# Revit family: RN 80035 Optipress-Aquaplus-Übergang
name_source: partatom
category: Rohrformteile
units: mm (PartAtom-declared; Revit-internal decimal feet)

## family parameters
Arbeitsebenenbasiert = Nein
Beim Laden mit Abzugskörper schneiden = Nein
Bemaßung runder Anschluss = Durchmesser verwenden
Gemeinsam genutzt = Nein
Immer vertikal = Ja
Teiletyp = Verbindung

## types (21) — shared parameters
1.010.00.2 Blattnummer der Richtlinie = 29
1.010.00.3 Ausgabedatum (Monat) der Richtlinie = 201308
1.010.00.4 Herstellername = R. Nussbaum AG
1.010.00.5 Revisionsdatum der Datei = 20190521
1.010.00.6 Webadresse des Herstellers = http://www.nussbaum.ch
1.100.00.4 Produktbezeichnung = Versorgung
1.110.00.2 Index = 4
1.110.00.4 Produktbezeichnung = Optipress
1.960/3L.00.8 Link (URL) = https://www.nussbaum.ch
29.700.00.4 Produktname = Optipress-Aquaplus-Übergang, mit Aussengewinde
29.700.00.5 Produktkennung = 2
29.700.00.6 Querschnittsform = 1
29.700.00.7 Nennweitensystem = DN
29.700.00.8 Nenndrucksystem = PN
29.710.02.4 Nenndruck = 16
29.710.02.5 max. zul. Überdruck [hPa] = 1600
29.710.02.7 max. zul. Dauer-Betriebsdruck [hPa] = 1600
29.710.02.9 max. zul. Dauer-Betriebstemperatur [°C] = 95
Connector Visibility = Nein
EnclosingSpace Visibility = Nein

## per-type parameters (varying)
- 80035.21, Optipress-Aquaplus-Übergang, mit Aussengewinde, DN=12x15, L=53, R=½: 1.800.00.3 TGA-Nummer=01900400000000000000000000000000000000000000000024000000000000000001; 1.810.00.3 Hersteller-Bestellnummer=80035.21; 1.810.00.4 DATANORM-Nummer=80035.21; 1.810.00.5 StLB-Nummer=267.112; 1.810.00.6 GTIN-Nummer=7612945051660; 29.710.02.10 Formstück-Gewicht [kg]=0.047; 29.710.02.3 Benennung=Optipress-Aquaplus-Übergang, mit Aussengewinde, DN=12x15, L=53, R=½; CONNECTOR0_DIAMETER_dX_0r=12 mm  [stored 0.0393701 ft]; CONNECTOR0_dX_01=22 mm; CONNECTOR0_ref_dX=22 mm; CONNECTOR1_DIAMETER_dX_0r=15 mm  [stored 0.0492126 ft]; CONNECTOR1_dX_00=40 mm  [stored 0.131234 ft]; CONNECTOR1_dX_01=53 mm; CONNECTOR1_ref_dX=40 mm  [stored 0.131234 ft]; R. Nussbaum AG 80035.21 de Visibility=Ja; R. Nussbaum AG 80035.22 de Visibility=Nein; R. Nussbaum AG 80035.23 de Visibility=Nein; R. Nussbaum AG 80035.24 de Visibility=Nein; R. Nussbaum AG 80035.25 de Visibility=Nein; R. Nussbaum AG 80035.27 de Visibility=Nein; R. Nussbaum AG 80035.28 de Visibility=Nein; R. Nussbaum AG 80035.29 de Visibility=Nein; R. Nussbaum AG 80035.30 de Visibility=Nein; R. Nussbaum AG 80035.31 de Visibility=Nein; R. Nussbaum AG 80035.32 de Visibility=Nein; R. Nussbaum AG 80035.33 de Visibility=Nein; R. Nussbaum AG 80035.34 de Visibility=Nein; R. Nussbaum AG 80035.35 de Visibility=Nein; R. Nussbaum AG 80035.36 de Visibility=Nein; R. Nussbaum AG 80035.37 de Visibility=Nein; R. Nussbaum AG 80035.38 de Visibility=Nein; R. Nussbaum AG 80035.70 de Visibility=Nein; R. Nussbaum AG 80035.71 de Visibility=Nein; R. Nussbaum AG 80035.72 de Visibility=Nein; R. Nussbaum AG 80035.73 de Visibility=Nein
- 80035.22, Optipress-Aquaplus-Übergang, mit Aussengewinde, DN=15x20, L=56, R=¾: 1.800.00.3 TGA-Nummer=01900400000000000000000000000000000000000000000024000000000000000002; 1.810.00.3 Hersteller-Bestellnummer=80035.22; 1.810.00.4 DATANORM-Nummer=80035.22; 1.810.00.6 GTIN-Nummer=7612945051677; 29.710.02.10 Formstück-Gewicht [kg]=0.058; 29.710.02.3 Benennung=Optipress-Aquaplus-Übergang, mit Aussengewinde, DN=15x20, L=56, R=¾; CONNECTOR0_DIAMETER_dX_0r=15 mm  [stored 0.0492126 ft]; CONNECTOR0_dX_01=22 mm; CONNECTOR0_ref_dX=22 mm; CONNECTOR1_DIAMETER_dX_0r=20 mm; CONNECTOR1_dX_00=41 mm  [stored 0.134514 ft]; CONNECTOR1_dX_01=56 mm; CONNECTOR1_ref_dX=41 mm  [stored 0.134514 ft]; R. Nussbaum AG 80035.21 de Visibility=Nein; R. Nussbaum AG 80035.22 de Visibility=Ja; R. Nussbaum AG 80035.23 de Visibility=Nein; R. Nussbaum AG 80035.24 de Visibility=Nein; R. Nussbaum AG 80035.25 de Visibility=Nein; R. Nussbaum AG 80035.27 de Visibility=Nein; R. Nussbaum AG 80035.28 de Visibility=Nein; R. Nussbaum AG 80035.29 de Visibility=Nein; R. Nussbaum AG 80035.30 de Visibility=Nein; R. Nussbaum AG 80035.31 de Visibility=Nein; R. Nussbaum AG 80035.32 de Visibility=Nein; R. Nussbaum AG 80035.33 de Visibility=Nein; R. Nussbaum AG 80035.34 de Visibility=Nein; R. Nussbaum AG 80035.35 de Visibility=Nein; R. Nussbaum AG 80035.36 de Visibility=Nein; R. Nussbaum AG 80035.37 de Visibility=Nein; R. Nussbaum AG 80035.38 de Visibility=Nein; R. Nussbaum AG 80035.70 de Visibility=Nein; R. Nussbaum AG 80035.71 de Visibility=Nein; R. Nussbaum AG 80035.72 de Visibility=Nein; R. Nussbaum AG 80035.73 de Visibility=Nein
- 80035.23, Optipress-Aquaplus-Übergang, mit Aussengewinde, DN=15, L=52, R=½: 1.800.00.3 TGA-Nummer=01900400000000000000000000000000000000000000000024000000000000000003; 1.810.00.3 Hersteller-Bestellnummer=80035.23; 1.810.00.4 DATANORM-Nummer=80035.23; 1.810.00.5 StLB-Nummer=267.113; 1.810.00.6 GTIN-Nummer=7612945051684; 29.710.02.10 Formstück-Gewicht [kg]=0.049; 29.710.02.3 Benennung=Optipress-Aquaplus-Übergang, mit Aussengewinde, DN=15, L=52, R=½; CONNECTOR0_DIAMETER_dX_0r=15 mm  [stored 0.0492126 ft]; CONNECTOR0_dX_01=22 mm; CONNECTOR0_ref_dX=22 mm; CONNECTOR1_DIAMETER_dX_0r=15 mm  [stored 0.0492126 ft]; CONNECTOR1_dX_00=39 mm; CONNECTOR1_dX_01=52 mm; CONNECTOR1_ref_dX=39 mm; R. Nussbaum AG 80035.21 de Visibility=Nein; R. Nussbaum AG 80035.22 de Visibility=Nein; R. Nussbaum AG 80035.23 de Visibility=Ja; R. Nussbaum AG 80035.24 de Visibility=Nein; R. Nussbaum AG 80035.25 de Visibility=Nein; R. Nussbaum AG 80035.27 de Visibility=Nein; R. Nussbaum AG 80035.28 de Visibility=Nein; R. Nussbaum AG 80035.29 de Visibility=Nein; R. Nussbaum AG 80035.30 de Visibility=Nein; R. Nussbaum AG 80035.31 de Visibility=Nein; R. Nussbaum AG 80035.32 de Visibility=Nein; R. Nussbaum AG 80035.33 de Visibility=Nein; R. Nussbaum AG 80035.34 de Visibility=Nein; R. Nussbaum AG 80035.35 de Visibility=Nein; R. Nussbaum AG 80035.36 de Visibility=Nein; R. Nussbaum AG 80035.37 de Visibility=Nein; R. Nussbaum AG 80035.38 de Visibility=Nein; R. Nussbaum AG 80035.70 de Visibility=Nein; R. Nussbaum AG 80035.71 de Visibility=Nein; R. Nussbaum AG 80035.72 de Visibility=Nein; R. Nussbaum AG 80035.73 de Visibility=Nein
- 80035.24, Optipress-Aquaplus-Übergang, mit Aussengewinde, DN=15x20, L=55, R=¾: 1.800.00.3 TGA-Nummer=01900400000000000000000000000000000000000000000024000000000000000004; 1.810.00.3 Hersteller-Bestellnummer=80035.24; 1.810.00.4 DATANORM-Nummer=80035.24; 1.810.00.6 GTIN-Nummer=7612945051691; 29.710.02.10 Formstück-Gewicht [kg]=0.064; 29.710.02.3 Benennung=Optipress-Aquaplus-Übergang, mit Aussengewinde, DN=15x20, L=55, R=¾; CONNECTOR0_DIAMETER_dX_0r=15 mm  [stored 0.0492126 ft]; CONNECTOR0_dX_01=22 mm; CONNECTOR0_ref_dX=22 mm; CONNECTOR1_DIAMETER_dX_0r=20 mm; CONNECTOR1_dX_00=40 mm  [stored 0.131234 ft]; CONNECTOR1_dX_01=55 mm; CONNECTOR1_ref_dX=40 mm  [stored 0.131234 ft]; R. Nussbaum AG 80035.21 de Visibility=Nein; R. Nussbaum AG 80035.22 de Visibility=Nein; R. Nussbaum AG 80035.23 de Visibility=Nein; R. Nussbaum AG 80035.24 de Visibility=Ja; R. Nussbaum AG 80035.25 de Visibility=Nein; R. Nussbaum AG 80035.27 de Visibility=Nein; R. Nussbaum AG 80035.28 de Visibility=Nein; R. Nussbaum AG 80035.29 de Visibility=Nein; R. Nussbaum AG 80035.30 de Visibility=Nein; R. Nussbaum AG 80035.31 de Visibility=Nein; R. Nussbaum AG 80035.32 de Visibility=Nein; R. Nussbaum AG 80035.33 de Visibility=Nein; R. Nussbaum AG 80035.34 de Visibility=Nein; R. Nussbaum AG 80035.35 de Visibility=Nein; R. Nussbaum AG 80035.36 de Visibility=Nein; R. Nussbaum AG 80035.37 de Visibility=Nein; R. Nussbaum AG 80035.38 de Visibility=Nein; R. Nussbaum AG 80035.70 de Visibility=Nein; R. Nussbaum AG 80035.71 de Visibility=Nein; R. Nussbaum AG 80035.72 de Visibility=Nein; R. Nussbaum AG 80035.73 de Visibility=Nein
- 80035.25, Optipress-Aquaplus-Übergang, mit Aussengewinde, DN=20, L=56, R=¾: 1.800.00.3 TGA-Nummer=01900400000000000000000000000000000000000000000024000000000000000005; 1.810.00.3 Hersteller-Bestellnummer=80035.25; 1.810.00.4 DATANORM-Nummer=80035.25; 1.810.00.5 StLB-Nummer=267.114; 1.810.00.6 GTIN-Nummer=7612945051714; 29.710.02.10 Formstück-Gewicht [kg]=0.069; 29.710.02.3 Benennung=Optipress-Aquaplus-Übergang, mit Aussengewinde, DN=20, L=56, R=¾; CONNECTOR0_DIAMETER_dX_0r=20 mm; CONNECTOR0_dX_01=24 mm; CONNECTOR0_ref_dX=24 mm; CONNECTOR1_DIAMETER_dX_0r=20 mm; CONNECTOR1_dX_00=41 mm  [stored 0.134514 ft]; CONNECTOR1_dX_01=56 mm; CONNECTOR1_ref_dX=41 mm  [stored 0.134514 ft]; R. Nussbaum AG 80035.21 de Visibility=Nein; R. Nussbaum AG 80035.22 de Visibility=Nein; R. Nussbaum AG 80035.23 de Visibility=Nein; R. Nussbaum AG 80035.24 de Visibility=Nein; R. Nussbaum AG 80035.25 de Visibility=Ja; R. Nussbaum AG 80035.27 de Visibility=Nein; R. Nussbaum AG 80035.28 de Visibility=Nein; R. Nussbaum AG 80035.29 de Visibility=Nein; R. Nussbaum AG 80035.30 de Visibility=Nein; R. Nussbaum AG 80035.31 de Visibility=Nein; R. Nussbaum AG 80035.32 de Visibility=Nein; R. Nussbaum AG 80035.33 de Visibility=Nein; R. Nussbaum AG 80035.34 de Visibility=Nein; R. Nussbaum AG 80035.35 de Visibility=Nein; R. Nussbaum AG 80035.36 de Visibility=Nein; R. Nussbaum AG 80035.37 de Visibility=Nein; R. Nussbaum AG 80035.38 de Visibility=Nein; R. Nussbaum AG 80035.70 de Visibility=Nein; R. Nussbaum AG 80035.71 de Visibility=Nein; R. Nussbaum AG 80035.72 de Visibility=Nein; R. Nussbaum AG 80035.73 de Visibility=Nein
- 80035.27, Optipress-Aquaplus-Übergang, mit Aussengewinde, DN=20x25, L=59, R=1: 1.800.00.3 TGA-Nummer=01900400000000000000000000000000000000000000000024000000000000000006; 1.810.00.3 Hersteller-Bestellnummer=80035.27; 1.810.00.4 DATANORM-Nummer=80035.27; 1.810.00.6 GTIN-Nummer=7612945051721; 29.710.02.10 Formstück-Gewicht [kg]=0.113; 29.710.02.3 Benennung=Optipress-Aquaplus-Übergang, mit Aussengewinde, DN=20x25, L=59, R=1; CONNECTOR0_DIAMETER_dX_0r=20 mm; CONNECTOR0_dX_01=24 mm; CONNECTOR0_ref_dX=24 mm; CONNECTOR1_DIAMETER_dX_0r=25 mm  [stored 0.082021 ft]; CONNECTOR1_dX_00=43 mm  [stored 0.141076 ft]; CONNECTOR1_dX_01=60 mm; CONNECTOR1_ref_dX=43 mm  [stored 0.141076 ft]; R. Nussbaum AG 80035.21 de Visibility=Nein; R. Nussbaum AG 80035.22 de Visibility=Nein; R. Nussbaum AG 80035.23 de Visibility=Nein; R. Nussbaum AG 80035.24 de Visibility=Nein; R. Nussbaum AG 80035.25 de Visibility=Nein; R. Nussbaum AG 80035.27 de Visibility=Ja; R. Nussbaum AG 80035.28 de Visibility=Nein; R. Nussbaum AG 80035.29 de Visibility=Nein; R. Nussbaum AG 80035.30 de Visibility=Nein; R. Nussbaum AG 80035.31 de Visibility=Nein; R. Nussbaum AG 80035.32 de Visibility=Nein; R. Nussbaum AG 80035.33 de Visibility=Nein; R. Nussbaum AG 80035.34 de Visibility=Nein; R. Nussbaum AG 80035.35 de Visibility=Nein; R. Nussbaum AG 80035.36 de Visibility=Nein; R. Nussbaum AG 80035.37 de Visibility=Nein; R. Nussbaum AG 80035.38 de Visibility=Nein; R. Nussbaum AG 80035.70 de Visibility=Nein; R. Nussbaum AG 80035.71 de Visibility=Nein; R. Nussbaum AG 80035.72 de Visibility=Nein; R. Nussbaum AG 80035.73 de Visibility=Nein
- 80035.28, Optipress-Aquaplus-Übergang, mit Aussengewinde, DN=25x20, L=57, R=¾: 1.800.00.3 TGA-Nummer=01900400000000000000000000000000000000000000000024000000000000000007; 1.810.00.3 Hersteller-Bestellnummer=80035.28; 1.810.00.4 DATANORM-Nummer=80035.28; 1.810.00.6 GTIN-Nummer=7612945051738; 29.710.02.10 Formstück-Gewicht [kg]=0.079; 29.710.02.3 Benennung=Optipress-Aquaplus-Übergang, mit Aussengewinde, DN=25x20, L=57, R=¾; CONNECTOR0_DIAMETER_dX_0r=25 mm  [stored 0.082021 ft]; CONNECTOR0_dX_01=24 mm; CONNECTOR0_ref_dX=24 mm; CONNECTOR1_DIAMETER_dX_0r=20 mm; CONNECTOR1_dX_00=42 mm; CONNECTOR1_dX_01=57 mm; CONNECTOR1_ref_dX=42 mm; R. Nussbaum AG 80035.21 de Visibility=Nein; R. Nussbaum AG 80035.22 de Visibility=Nein; R. Nussbaum AG 80035.23 de Visibility=Nein; R. Nussbaum AG 80035.24 de Visibility=Nein; R. Nussbaum AG 80035.25 de Visibility=Nein; R. Nussbaum AG 80035.27 de Visibility=Nein; R. Nussbaum AG 80035.28 de Visibility=Ja; R. Nussbaum AG 80035.29 de Visibility=Nein; R. Nussbaum AG 80035.30 de Visibility=Nein; R. Nussbaum AG 80035.31 de Visibility=Nein; R. Nussbaum AG 80035.32 de Visibility=Nein; R. Nussbaum AG 80035.33 de Visibility=Nein; R. Nussbaum AG 80035.34 de Visibility=Nein; R. Nussbaum AG 80035.35 de Visibility=Nein; R. Nussbaum AG 80035.36 de Visibility=Nein; R. Nussbaum AG 80035.37 de Visibility=Nein; R. Nussbaum AG 80035.38 de Visibility=Nein; R. Nussbaum AG 80035.70 de Visibility=Nein; R. Nussbaum AG 80035.71 de Visibility=Nein; R. Nussbaum AG 80035.72 de Visibility=Nein; R. Nussbaum AG 80035.73 de Visibility=Nein
- 80035.29, Optipress-Aquaplus-Übergang, mit Aussengewinde, DN=25, L=61, R=1: 1.800.00.3 TGA-Nummer=01900400000000000000000000000000000000000000000024000000000000000008; 1.810.00.3 Hersteller-Bestellnummer=80035.29; 1.810.00.4 DATANORM-Nummer=80035.29; 1.810.00.5 StLB-Nummer=267.115; 1.810.00.6 GTIN-Nummer=7612945051745; 29.710.02.10 Formstück-Gewicht [kg]=0.121; 29.710.02.3 Benennung=Optipress-Aquaplus-Übergang, mit Aussengewinde, DN=25, L=61, R=1; CONNECTOR0_DIAMETER_dX_0r=25 mm  [stored 0.082021 ft]; CONNECTOR0_dX_01=24 mm; CONNECTOR0_ref_dX=24 mm; CONNECTOR1_DIAMETER_dX_0r=25 mm  [stored 0.082021 ft]; CONNECTOR1_dX_00=44 mm; CONNECTOR1_dX_01=61 mm; CONNECTOR1_ref_dX=44 mm; R. Nussbaum AG 80035.21 de Visibility=Nein; R. Nussbaum AG 80035.22 de Visibility=Nein; R. Nussbaum AG 80035.23 de Visibility=Nein; R. Nussbaum AG 80035.24 de Visibility=Nein; R. Nussbaum AG 80035.25 de Visibility=Nein; R. Nussbaum AG 80035.27 de Visibility=Nein; R. Nussbaum AG 80035.28 de Visibility=Nein; R. Nussbaum AG 80035.29 de Visibility=Ja; R. Nussbaum AG 80035.30 de Visibility=Nein; R. Nussbaum AG 80035.31 de Visibility=Nein; R. Nussbaum AG 80035.32 de Visibility=Nein; R. Nussbaum AG 80035.33 de Visibility=Nein; R. Nussbaum AG 80035.34 de Visibility=Nein; R. Nussbaum AG 80035.35 de Visibility=Nein; R. Nussbaum AG 80035.36 de Visibility=Nein; R. Nussbaum AG 80035.37 de Visibility=Nein; R. Nussbaum AG 80035.38 de Visibility=Nein; R. Nussbaum AG 80035.70 de Visibility=Nein; R. Nussbaum AG 80035.71 de Visibility=Nein; R. Nussbaum AG 80035.72 de Visibility=Nein; R. Nussbaum AG 80035.73 de Visibility=Nein
- 80035.31, Optipress-Aquaplus-Übergang, mit Aussengewinde, DN=32, L=69, R=1¼: 1.800.00.3 TGA-Nummer=01900400000000000000000000000000000000000000000024000000000000000009; 1.810.00.3 Hersteller-Bestellnummer=80035.31; 1.810.00.4 DATANORM-Nummer=80035.31; 1.810.00.5 StLB-Nummer=267.116; 1.810.00.6 GTIN-Nummer=7612945051769; 29.710.02.10 Formstück-Gewicht [kg]=0.229; 29.710.02.3 Benennung=Optipress-Aquaplus-Übergang, mit Aussengewinde, DN=32, L=69, R=1¼; CONNECTOR0_DIAMETER_dX_0r=32 mm  [stored 0.104987 ft]; CONNECTOR0_dX_01=26 mm; CONNECTOR0_ref_dX=26 mm; CONNECTOR1_DIAMETER_dX_0r=32 mm  [stored 0.104987 ft]; CONNECTOR1_dX_00=50 mm; CONNECTOR1_dX_01=69 mm; CONNECTOR1_ref_dX=50 mm; R. Nussbaum AG 80035.21 de Visibility=Nein; R. Nussbaum AG 80035.22 de Visibility=Nein; R. Nussbaum AG 80035.23 de Visibility=Nein; R. Nussbaum AG 80035.24 de Visibility=Nein; R. Nussbaum AG 80035.25 de Visibility=Nein; R. Nussbaum AG 80035.27 de Visibility=Nein; R. Nussbaum AG 80035.28 de Visibility=Nein; R. Nussbaum AG 80035.29 de Visibility=Nein; R. Nussbaum AG 80035.30 de Visibility=Nein; R. Nussbaum AG 80035.31 de Visibility=Ja; R. Nussbaum AG 80035.32 de Visibility=Nein; R. Nussbaum AG 80035.33 de Visibility=Nein; R. Nussbaum AG 80035.34 de Visibility=Nein; R. Nussbaum AG 80035.35 de Visibility=Nein; R. Nussbaum AG 80035.36 de Visibility=Nein; R. Nussbaum AG 80035.37 de Visibility=Nein; R. Nussbaum AG 80035.38 de Visibility=Nein; R. Nussbaum AG 80035.70 de Visibility=Nein; R. Nussbaum AG 80035.71 de Visibility=Nein; R. Nussbaum AG 80035.72 de Visibility=Nein; R. Nussbaum AG 80035.73 de Visibility=Nein
- 80035.32, Optipress-Aquaplus-Übergang, mit Aussengewinde, DN=32x40, L=70, R=1½: 1.800.00.3 TGA-Nummer=01900400000000000000000000000000000000000000000024000000000000000010; 1.810.00.3 Hersteller-Bestellnummer=80035.32; 1.810.00.4 DATANORM-Nummer=80035.32; 1.810.00.6 GTIN-Nummer=7612945709875; 29.710.02.10 Formstück-Gewicht [kg]=0.001; 29.710.02.3 Benennung=Optipress-Aquaplus-Übergang, mit Aussengewinde, DN=32x40, L=70, R=1½; CONNECTOR0_DIAMETER_dX_0r=32 mm  [stored 0.104987 ft]; CONNECTOR0_dX_01=26 mm; CONNECTOR0_ref_dX=26 mm; CONNECTOR1_DIAMETER_dX_0r=40 mm  [stored 0.131234 ft]; CONNECTOR1_dX_00=51 mm; CONNECTOR1_dX_01=70 mm; CONNECTOR1_ref_dX=51 mm; R. Nussbaum AG 80035.21 de Visibility=Nein; R. Nussbaum AG 80035.22 de Visibility=Nein; R. Nussbaum AG 80035.23 de Visibility=Nein; R. Nussbaum AG 80035.24 de Visibility=Nein; R. Nussbaum AG 80035.25 de Visibility=Nein; R. Nussbaum AG 80035.27 de Visibility=Nein; R. Nussbaum AG 80035.28 de Visibility=Nein; R. Nussbaum AG 80035.29 de Visibility=Nein; R. Nussbaum AG 80035.30 de Visibility=Nein; R. Nussbaum AG 80035.31 de Visibility=Nein; R. Nussbaum AG 80035.32 de Visibility=Ja; R. Nussbaum AG 80035.33 de Visibility=Nein; R. Nussbaum AG 80035.34 de Visibility=Nein; R. Nussbaum AG 80035.35 de Visibility=Nein; R. Nussbaum AG 80035.36 de Visibility=Nein; R. Nussbaum AG 80035.37 de Visibility=Nein; R. Nussbaum AG 80035.38 de Visibility=Nein; R. Nussbaum AG 80035.70 de Visibility=Nein; R. Nussbaum AG 80035.71 de Visibility=Nein; R. Nussbaum AG 80035.72 de Visibility=Nein; R. Nussbaum AG 80035.73 de Visibility=Nein
- 80035.33, Optipress-Aquaplus-Übergang, mit Aussengewinde, DN=40, L=81, R=1½: 1.800.00.3 TGA-Nummer=01900400000000000000000000000000000000000000000024000000000000000011; 1.810.00.3 Hersteller-Bestellnummer=80035.33; 1.810.00.4 DATANORM-Nummer=80035.33; 1.810.00.5 StLB-Nummer=267.117; 1.810.00.6 GTIN-Nummer=7612945051776; 29.710.02.10 Formstück-Gewicht [kg]=0.283; 29.710.02.3 Benennung=Optipress-Aquaplus-Übergang, mit Aussengewinde, DN=40, L=81, R=1½; CONNECTOR0_DIAMETER_dX_0r=40 mm  [stored 0.131234 ft]; CONNECTOR0_dX_01=36 mm  [stored 0.11811 ft]; CONNECTOR0_ref_dX=36 mm  [stored 0.11811 ft]; CONNECTOR1_DIAMETER_dX_0r=40 mm  [stored 0.131234 ft]; CONNECTOR1_dX_00=62 mm; CONNECTOR1_dX_01=81 mm; CONNECTOR1_ref_dX=62 mm; R. Nussbaum AG 80035.21 de Visibility=Nein; R. Nussbaum AG 80035.22 de Visibility=Nein; R. Nussbaum AG 80035.23 de Visibility=Nein; R. Nussbaum AG 80035.24 de Visibility=Nein; R. Nussbaum AG 80035.25 de Visibility=Nein; R. Nussbaum AG 80035.27 de Visibility=Nein; R. Nussbaum AG 80035.28 de Visibility=Nein; R. Nussbaum AG 80035.29 de Visibility=Nein; R. Nussbaum AG 80035.30 de Visibility=Nein; R. Nussbaum AG 80035.31 de Visibility=Nein; R. Nussbaum AG 80035.32 de Visibility=Nein; R. Nussbaum AG 80035.33 de Visibility=Ja; R. Nussbaum AG 80035.34 de Visibility=Nein; R. Nussbaum AG 80035.35 de Visibility=Nein; R. Nussbaum AG 80035.36 de Visibility=Nein; R. Nussbaum AG 80035.37 de Visibility=Nein; R. Nussbaum AG 80035.38 de Visibility=Nein; R. Nussbaum AG 80035.70 de Visibility=Nein; R. Nussbaum AG 80035.71 de Visibility=Nein; R. Nussbaum AG 80035.72 de Visibility=Nein; R. Nussbaum AG 80035.73 de Visibility=Nein
- 80035.34, Optipress-Aquaplus-Übergang, mit Aussengewinde, DN=50, L=89, R=2: 1.800.00.3 TGA-Nummer=01900400000000000000000000000000000000000000000024000000000000000012; 1.810.00.3 Hersteller-Bestellnummer=80035.34; 1.810.00.4 DATANORM-Nummer=80035.34; 1.810.00.5 StLB-Nummer=267.118; 1.810.00.6 GTIN-Nummer=7612945051783; 29.710.02.10 Formstück-Gewicht [kg]=0.376; 29.710.02.3 Benennung=Optipress-Aquaplus-Übergang, mit Aussengewinde, DN=50, L=89, R=2; CONNECTOR0_DIAMETER_dX_0r=50 mm; CONNECTOR0_dX_01=40 mm  [stored 0.131234 ft]; CONNECTOR0_ref_dX=40 mm  [stored 0.131234 ft]; CONNECTOR1_DIAMETER_dX_0r=50 mm; CONNECTOR1_dX_00=65 mm; CONNECTOR1_dX_01=89 mm; CONNECTOR1_ref_dX=65 mm; R. Nussbaum AG 80035.21 de Visibility=Nein; R. Nussbaum AG 80035.22 de Visibility=Nein; R. Nussbaum AG 80035.23 de Visibility=Nein; R. Nussbaum AG 80035.24 de Visibility=Nein; R. Nussbaum AG 80035.25 de Visibility=Nein; R. Nussbaum AG 80035.27 de Visibility=Nein; R. Nussbaum AG 80035.28 de Visibility=Nein; R. Nussbaum AG 80035.29 de Visibility=Nein; R. Nussbaum AG 80035.30 de Visibility=Nein; R. Nussbaum AG 80035.31 de Visibility=Nein; R. Nussbaum AG 80035.32 de Visibility=Nein; R. Nussbaum AG 80035.33 de Visibility=Nein; R. Nussbaum AG 80035.34 de Visibility=Ja; R. Nussbaum AG 80035.35 de Visibility=Nein; R. Nussbaum AG 80035.36 de Visibility=Nein; R. Nussbaum AG 80035.37 de Visibility=Nein; R. Nussbaum AG 80035.38 de Visibility=Nein; R. Nussbaum AG 80035.70 de Visibility=Nein; R. Nussbaum AG 80035.71 de Visibility=Nein; R. Nussbaum AG 80035.72 de Visibility=Nein; R. Nussbaum AG 80035.73 de Visibility=Nein
- 80035.35, Optipress-Aquaplus-Übergang, mit Aussengewinde, DN=40x32, L=81, R=1¼: 1.800.00.3 TGA-Nummer=01900400000000000000000000000000000000000000000024000000000000000013; 1.810.00.3 Hersteller-Bestellnummer=80035.35; 1.810.00.4 DATANORM-Nummer=80035.35; 1.810.00.6 GTIN-Nummer=7612945709882; 29.710.02.10 Formstück-Gewicht [kg]=0.244; 29.710.02.3 Benennung=Optipress-Aquaplus-Übergang, mit Aussengewinde, DN=40x32, L=81, R=1¼; CONNECTOR0_DIAMETER_dX_0r=40 mm  [stored 0.131234 ft]; CONNECTOR0_dX_01=36 mm  [stored 0.11811 ft]; CONNECTOR0_ref_dX=36 mm  [stored 0.11811 ft]; CONNECTOR1_DIAMETER_dX_0r=32 mm  [stored 0.104987 ft]; CONNECTOR1_dX_00=62 mm; CONNECTOR1_dX_01=81 mm; CONNECTOR1_ref_dX=62 mm; R. Nussbaum AG 80035.21 de Visibility=Nein; R. Nussbaum AG 80035.22 de Visibility=Nein; R. Nussbaum AG 80035.23 de Visibility=Nein; R. Nussbaum AG 80035.24 de Visibility=Nein; R. Nussbaum AG 80035.25 de Visibility=Nein; R. Nussbaum AG 80035.27 de Visibility=Nein; R. Nussbaum AG 80035.28 de Visibility=Nein; R. Nussbaum AG 80035.29 de Visibility=Nein; R. Nussbaum AG 80035.30 de Visibility=Nein; R. Nussbaum AG 80035.31 de Visibility=Nein; R. Nussbaum AG 80035.32 de Visibility=Nein; R. Nussbaum AG 80035.33 de Visibility=Nein; R. Nussbaum AG 80035.34 de Visibility=Nein; R. Nussbaum AG 80035.35 de Visibility=Ja; R. Nussbaum AG 80035.36 de Visibility=Nein; R. Nussbaum AG 80035.37 de Visibility=Nein; R. Nussbaum AG 80035.38 de Visibility=Nein; R. Nussbaum AG 80035.70 de Visibility=Nein; R. Nussbaum AG 80035.71 de Visibility=Nein; R. Nussbaum AG 80035.72 de Visibility=Nein; R. Nussbaum AG 80035.73 de Visibility=Nein
- 80035.36, Optipress-Aquaplus-Übergang, mit Aussengewinde, DN=20x15, L=54, R=½: 1.800.00.3 TGA-Nummer=01900400000000000000000000000000000000000000000024000000000000000014; 1.810.00.3 Hersteller-Bestellnummer=80035.36; 1.810.00.4 DATANORM-Nummer=80035.36; 1.810.00.6 GTIN-Nummer=7612945051707; 29.710.02.10 Formstück-Gewicht [kg]=0.062; 29.710.02.3 Benennung=Optipress-Aquaplus-Übergang, mit Aussengewinde, DN=20x15, L=54, R=½; CONNECTOR0_DIAMETER_dX_0r=20 mm; CONNECTOR0_dX_01=24 mm; CONNECTOR0_ref_dX=24 mm; CONNECTOR1_DIAMETER_dX_0r=15 mm  [stored 0.0492126 ft]; CONNECTOR1_dX_00=41 mm  [stored 0.134514 ft]; CONNECTOR1_dX_01=54 mm; CONNECTOR1_ref_dX=41 mm  [stored 0.134514 ft]; R. Nussbaum AG 80035.21 de Visibility=Nein; R. Nussbaum AG 80035.22 de Visibility=Nein; R. Nussbaum AG 80035.23 de Visibility=Nein; R. Nussbaum AG 80035.24 de Visibility=Nein; R. Nussbaum AG 80035.25 de Visibility=Nein; R. Nussbaum AG 80035.27 de Visibility=Nein; R. Nussbaum AG 80035.28 de Visibility=Nein; R. Nussbaum AG 80035.29 de Visibility=Nein; R. Nussbaum AG 80035.30 de Visibility=Nein; R. Nussbaum AG 80035.31 de Visibility=Nein; R. Nussbaum AG 80035.32 de Visibility=Nein; R. Nussbaum AG 80035.33 de Visibility=Nein; R. Nussbaum AG 80035.34 de Visibility=Nein; R. Nussbaum AG 80035.35 de Visibility=Nein; R. Nussbaum AG 80035.36 de Visibility=Ja; R. Nussbaum AG 80035.37 de Visibility=Nein; R. Nussbaum AG 80035.38 de Visibility=Nein; R. Nussbaum AG 80035.70 de Visibility=Nein; R. Nussbaum AG 80035.71 de Visibility=Nein; R. Nussbaum AG 80035.72 de Visibility=Nein; R. Nussbaum AG 80035.73 de Visibility=Nein
- 80035.37, Optipress-Aquaplus-Übergang, mit Aussengewinde, DN=32x25, L=64, R=1: 1.800.00.3 TGA-Nummer=01900400000000000000000000000000000000000000000024000000000000000015; 1.810.00.3 Hersteller-Bestellnummer=80035.37; 1.810.00.4 DATANORM-Nummer=80035.37; 1.810.00.6 GTIN-Nummer=7612945051752; 29.710.02.10 Formstück-Gewicht [kg]=0.12; 29.710.02.3 Benennung=Optipress-Aquaplus-Übergang, mit Aussengewinde, DN=32x25, L=64, R=1; CONNECTOR0_DIAMETER_dX_0r=32 mm  [stored 0.104987 ft]; CONNECTOR0_dX_01=26 mm; CONNECTOR0_ref_dX=26 mm; CONNECTOR1_DIAMETER_dX_0r=25 mm  [stored 0.082021 ft]; CONNECTOR1_dX_00=44 mm; CONNECTOR1_dX_01=64 mm; CONNECTOR1_ref_dX=44 mm; R. Nussbaum AG 80035.21 de Visibility=Nein; R. Nussbaum AG 80035.22 de Visibility=Nein; R. Nussbaum AG 80035.23 de Visibility=Nein; R. Nussbaum AG 80035.24 de Visibility=Nein; R. Nussbaum AG 80035.25 de Visibility=Nein; R. Nussbaum AG 80035.27 de Visibility=Nein; R. Nussbaum AG 80035.28 de Visibility=Nein; R. Nussbaum AG 80035.29 de Visibility=Nein; R. Nussbaum AG 80035.30 de Visibility=Nein; R. Nussbaum AG 80035.31 de Visibility=Nein; R. Nussbaum AG 80035.32 de Visibility=Nein; R. Nussbaum AG 80035.33 de Visibility=Nein; R. Nussbaum AG 80035.34 de Visibility=Nein; R. Nussbaum AG 80035.35 de Visibility=Nein; R. Nussbaum AG 80035.36 de Visibility=Nein; R. Nussbaum AG 80035.37 de Visibility=Ja; R. Nussbaum AG 80035.38 de Visibility=Nein; R. Nussbaum AG 80035.70 de Visibility=Nein; R. Nussbaum AG 80035.71 de Visibility=Nein; R. Nussbaum AG 80035.72 de Visibility=Nein; R. Nussbaum AG 80035.73 de Visibility=Nein
- 80035.38, Optipress-Aquaplus-Übergang, mit Aussengewinde, DN=50x40, L=90, R=1½: 1.800.00.3 TGA-Nummer=01900400000000000000000000000000000000000000000024000000000000000016; 1.810.00.3 Hersteller-Bestellnummer=80035.38; 1.810.00.4 DATANORM-Nummer=80035.38; 1.810.00.6 GTIN-Nummer=7612945709899; 29.710.02.10 Formstück-Gewicht [kg]=0.391; 29.710.02.3 Benennung=Optipress-Aquaplus-Übergang, mit Aussengewinde, DN=50x40, L=90, R=1½; CONNECTOR0_DIAMETER_dX_0r=50 mm; CONNECTOR0_dX_01=40 mm  [stored 0.131234 ft]; CONNECTOR0_ref_dX=40 mm  [stored 0.131234 ft]; CONNECTOR1_DIAMETER_dX_0r=40 mm  [stored 0.131234 ft]; CONNECTOR1_dX_00=71 mm; CONNECTOR1_dX_01=90 mm; CONNECTOR1_ref_dX=71 mm; R. Nussbaum AG 80035.21 de Visibility=Nein; R. Nussbaum AG 80035.22 de Visibility=Nein; R. Nussbaum AG 80035.23 de Visibility=Nein; R. Nussbaum AG 80035.24 de Visibility=Nein; R. Nussbaum AG 80035.25 de Visibility=Nein; R. Nussbaum AG 80035.27 de Visibility=Nein; R. Nussbaum AG 80035.28 de Visibility=Nein; R. Nussbaum AG 80035.29 de Visibility=Nein; R. Nussbaum AG 80035.30 de Visibility=Nein; R. Nussbaum AG 80035.31 de Visibility=Nein; R. Nussbaum AG 80035.32 de Visibility=Nein; R. Nussbaum AG 80035.33 de Visibility=Nein; R. Nussbaum AG 80035.34 de Visibility=Nein; R. Nussbaum AG 80035.35 de Visibility=Nein; R. Nussbaum AG 80035.36 de Visibility=Nein; R. Nussbaum AG 80035.37 de Visibility=Nein; R. Nussbaum AG 80035.38 de Visibility=Ja; R. Nussbaum AG 80035.70 de Visibility=Nein; R. Nussbaum AG 80035.71 de Visibility=Nein; R. Nussbaum AG 80035.72 de Visibility=Nein; R. Nussbaum AG 80035.73 de Visibility=Nein
- 80035.71, Optipress-Aquaplus-Übergang, mit Aussengewinde, DN=65, L=115, R=2½: 1.800.00.3 TGA-Nummer=01900400000000000000000000000000000000000000000024000000000000000017; 1.810.00.3 Hersteller-Bestellnummer=80035.71; 1.810.00.4 DATANORM-Nummer=80035.71; 1.810.00.5 StLB-Nummer=267.121; 1.810.00.6 GTIN-Nummer=7612945655370; 29.710.02.10 Formstück-Gewicht [kg]=0.87; 29.710.02.3 Benennung=Optipress-Aquaplus-Übergang, mit Aussengewinde, DN=65, L=115, R=2½; CONNECTOR0_DIAMETER_dX_0r=65 mm; CONNECTOR0_dX_01=50 mm; CONNECTOR0_ref_dX=50 mm; CONNECTOR1_DIAMETER_dX_0r=65 mm; CONNECTOR1_dX_00=88 mm; CONNECTOR1_dX_01=115 mm; CONNECTOR1_ref_dX=88 mm; R. Nussbaum AG 80035.21 de Visibility=Nein; R. Nussbaum AG 80035.22 de Visibility=Nein; R. Nussbaum AG 80035.23 de Visibility=Nein; R. Nussbaum AG 80035.24 de Visibility=Nein; R. Nussbaum AG 80035.25 de Visibility=Nein; R. Nussbaum AG 80035.27 de Visibility=Nein; R. Nussbaum AG 80035.28 de Visibility=Nein; R. Nussbaum AG 80035.29 de Visibility=Nein; R. Nussbaum AG 80035.30 de Visibility=Nein; R. Nussbaum AG 80035.31 de Visibility=Nein; R. Nussbaum AG 80035.32 de Visibility=Nein; R. Nussbaum AG 80035.33 de Visibility=Nein; R. Nussbaum AG 80035.34 de Visibility=Nein; R. Nussbaum AG 80035.35 de Visibility=Nein; R. Nussbaum AG 80035.36 de Visibility=Nein; R. Nussbaum AG 80035.37 de Visibility=Nein; R. Nussbaum AG 80035.38 de Visibility=Nein; R. Nussbaum AG 80035.70 de Visibility=Nein; R. Nussbaum AG 80035.71 de Visibility=Ja; R. Nussbaum AG 80035.72 de Visibility=Nein; R. Nussbaum AG 80035.73 de Visibility=Nein
- 80035.72, Optipress-Aquaplus-Übergang, mit Aussengewinde, DN=80, L=119, R=3: 1.800.00.3 TGA-Nummer=01900400000000000000000000000000000000000000000024000000000000000018; 1.810.00.3 Hersteller-Bestellnummer=80035.72; 1.810.00.4 DATANORM-Nummer=80035.72; 1.810.00.5 StLB-Nummer=267.122; 1.810.00.6 GTIN-Nummer=7612945655387; 29.710.02.10 Formstück-Gewicht [kg]=1.079; 29.710.02.3 Benennung=Optipress-Aquaplus-Übergang, mit Aussengewinde, DN=80, L=119, R=3; CONNECTOR0_DIAMETER_dX_0r=80 mm; CONNECTOR0_dX_01=50 mm; CONNECTOR0_ref_dX=50 mm; CONNECTOR1_DIAMETER_dX_0r=80 mm; CONNECTOR1_dX_00=88 mm; CONNECTOR1_dX_01=118 mm; CONNECTOR1_ref_dX=88 mm; R. Nussbaum AG 80035.21 de Visibility=Nein; R. Nussbaum AG 80035.22 de Visibility=Nein; R. Nussbaum AG 80035.23 de Visibility=Nein; R. Nussbaum AG 80035.24 de Visibility=Nein; R. Nussbaum AG 80035.25 de Visibility=Nein; R. Nussbaum AG 80035.27 de Visibility=Nein; R. Nussbaum AG 80035.28 de Visibility=Nein; R. Nussbaum AG 80035.29 de Visibility=Nein; R. Nussbaum AG 80035.30 de Visibility=Nein; R. Nussbaum AG 80035.31 de Visibility=Nein; R. Nussbaum AG 80035.32 de Visibility=Nein; R. Nussbaum AG 80035.33 de Visibility=Nein; R. Nussbaum AG 80035.34 de Visibility=Nein; R. Nussbaum AG 80035.35 de Visibility=Nein; R. Nussbaum AG 80035.36 de Visibility=Nein; R. Nussbaum AG 80035.37 de Visibility=Nein; R. Nussbaum AG 80035.38 de Visibility=Nein; R. Nussbaum AG 80035.70 de Visibility=Nein; R. Nussbaum AG 80035.71 de Visibility=Nein; R. Nussbaum AG 80035.72 de Visibility=Ja; R. Nussbaum AG 80035.73 de Visibility=Nein
- 80035.73, Optipress-Aquaplus-Übergang, mit Aussengewinde, DN=100, L=135, R=4: 1.800.00.3 TGA-Nummer=01900400000000000000000000000000000000000000000024000000000000000019; 1.810.00.3 Hersteller-Bestellnummer=80035.73; 1.810.00.4 DATANORM-Nummer=80035.73; 1.810.00.5 StLB-Nummer=267.123; 1.810.00.6 GTIN-Nummer=7612945655394; 29.710.02.10 Formstück-Gewicht [kg]=1.599; 29.710.02.3 Benennung=Optipress-Aquaplus-Übergang, mit Aussengewinde, DN=100, L=135, R=4; CONNECTOR0_DIAMETER_dX_0r=100 mm; CONNECTOR0_dX_01=60 mm; CONNECTOR0_ref_dX=60 mm; CONNECTOR1_DIAMETER_dX_0r=100 mm; CONNECTOR1_dX_00=98 mm; CONNECTOR1_dX_01=134 mm; CONNECTOR1_ref_dX=98 mm; R. Nussbaum AG 80035.21 de Visibility=Nein; R. Nussbaum AG 80035.22 de Visibility=Nein; R. Nussbaum AG 80035.23 de Visibility=Nein; R. Nussbaum AG 80035.24 de Visibility=Nein; R. Nussbaum AG 80035.25 de Visibility=Nein; R. Nussbaum AG 80035.27 de Visibility=Nein; R. Nussbaum AG 80035.28 de Visibility=Nein; R. Nussbaum AG 80035.29 de Visibility=Nein; R. Nussbaum AG 80035.30 de Visibility=Nein; R. Nussbaum AG 80035.31 de Visibility=Nein; R. Nussbaum AG 80035.32 de Visibility=Nein; R. Nussbaum AG 80035.33 de Visibility=Nein; R. Nussbaum AG 80035.34 de Visibility=Nein; R. Nussbaum AG 80035.35 de Visibility=Nein; R. Nussbaum AG 80035.36 de Visibility=Nein; R. Nussbaum AG 80035.37 de Visibility=Nein; R. Nussbaum AG 80035.38 de Visibility=Nein; R. Nussbaum AG 80035.70 de Visibility=Nein; R. Nussbaum AG 80035.71 de Visibility=Nein; R. Nussbaum AG 80035.72 de Visibility=Nein; R. Nussbaum AG 80035.73 de Visibility=Ja
- 80035.30, Optipress-Aquaplus-Übergang, mit Aussengewinde, DN=25x32, L=68, R=1¼: 1.800.00.3 TGA-Nummer=01900400000000000000000000000000000000000000000024000000000000000038; 1.810.00.3 Hersteller-Bestellnummer=80035.30; 1.810.00.4 DATANORM-Nummer=80035.30; 1.810.00.6 GTIN-Nummer=7612945709868; 29.710.02.10 Formstück-Gewicht [kg]=0.228; 29.710.02.3 Benennung=Optipress-Aquaplus-Übergang, mit Aussengewinde, DN=25x32, L=68, R=1¼; CONNECTOR0_DIAMETER_dX_0r=25 mm  [stored 0.082021 ft]; CONNECTOR0_dX_01=24 mm; CONNECTOR0_ref_dX=24 mm; CONNECTOR1_DIAMETER_dX_0r=32 mm  [stored 0.104987 ft]; CONNECTOR1_dX_00=49 mm; CONNECTOR1_dX_01=68 mm; CONNECTOR1_ref_dX=49 mm; R. Nussbaum AG 80035.21 de Visibility=Nein; R. Nussbaum AG 80035.22 de Visibility=Nein; R. Nussbaum AG 80035.23 de Visibility=Nein; R. Nussbaum AG 80035.24 de Visibility=Nein; R. Nussbaum AG 80035.25 de Visibility=Nein; R. Nussbaum AG 80035.27 de Visibility=Nein; R. Nussbaum AG 80035.28 de Visibility=Nein; R. Nussbaum AG 80035.29 de Visibility=Nein; R. Nussbaum AG 80035.30 de Visibility=Ja; R. Nussbaum AG 80035.31 de Visibility=Nein; R. Nussbaum AG 80035.32 de Visibility=Nein; R. Nussbaum AG 80035.33 de Visibility=Nein; R. Nussbaum AG 80035.34 de Visibility=Nein; R. Nussbaum AG 80035.35 de Visibility=Nein; R. Nussbaum AG 80035.36 de Visibility=Nein; R. Nussbaum AG 80035.37 de Visibility=Nein; R. Nussbaum AG 80035.38 de Visibility=Nein; R. Nussbaum AG 80035.70 de Visibility=Nein; R. Nussbaum AG 80035.71 de Visibility=Nein; R. Nussbaum AG 80035.72 de Visibility=Nein; R. Nussbaum AG 80035.73 de Visibility=Nein
- 80035.70, Optipress-Aquaplus-Übergang, mit Aussengewinde, DN=60x65, L=109, R=2½: 1.800.00.3 TGA-Nummer=01900400000000000000000000000000000000000000000024000000000000000039; 1.810.00.3 Hersteller-Bestellnummer=80035.70; 1.810.00.4 DATANORM-Nummer=80035.70; 1.810.00.5 StLB-Nummer=267.124; 1.810.00.6 GTIN-Nummer=7612945682505; 29.710.02.10 Formstück-Gewicht [kg]=0.956; 29.710.02.3 Benennung=Optipress-Aquaplus-Übergang, mit Aussengewinde, DN=60x65, L=109, R=2½; CONNECTOR0_DIAMETER_dX_0r=60 mm; CONNECTOR0_dX_01=43 mm  [stored 0.141076 ft]; CONNECTOR0_ref_dX=43 mm  [stored 0.141076 ft]; CONNECTOR1_DIAMETER_dX_0r=65 mm; CONNECTOR1_dX_00=82 mm; CONNECTOR1_dX_01=109 mm; CONNECTOR1_ref_dX=82 mm; R. Nussbaum AG 80035.21 de Visibility=Nein; R. Nussbaum AG 80035.22 de Visibility=Nein; R. Nussbaum AG 80035.23 de Visibility=Nein; R. Nussbaum AG 80035.24 de Visibility=Nein; R. Nussbaum AG 80035.25 de Visibility=Nein; R. Nussbaum AG 80035.27 de Visibility=Nein; R. Nussbaum AG 80035.28 de Visibility=Nein; R. Nussbaum AG 80035.29 de Visibility=Nein; R. Nussbaum AG 80035.30 de Visibility=Nein; R. Nussbaum AG 80035.31 de Visibility=Nein; R. Nussbaum AG 80035.32 de Visibility=Nein; R. Nussbaum AG 80035.33 de Visibility=Nein; R. Nussbaum AG 80035.34 de Visibility=Nein; R. Nussbaum AG 80035.35 de Visibility=Nein; R. Nussbaum AG 80035.36 de Visibility=Nein; R. Nussbaum AG 80035.37 de Visibility=Nein; R. Nussbaum AG 80035.38 de Visibility=Nein; R. Nussbaum AG 80035.70 de Visibility=Ja; R. Nussbaum AG 80035.71 de Visibility=Nein; R. Nussbaum AG 80035.72 de Visibility=Nein; R. Nussbaum AG 80035.73 de Visibility=Nein

note: column(s) folded — value = type name in every type: 1.800.00.4 Kommentarfeld

note: [stored X ft] marks values corroborated as IEEE doubles in the binary element streams (Revit-internal decimal feet)

## geometry (parser evidence)
native form markers: Sweep x3
no freeform markers — native parametric forms only
